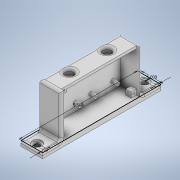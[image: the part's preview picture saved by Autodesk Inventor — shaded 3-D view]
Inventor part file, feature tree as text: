
AUTODESK INVENTOR PART (.ipt)
format: ipt  version: 2020 (Build 240168000, 168)  size: 391,680 bytes
history: native  units: in
note: dims shown in document units (in); Inventor stores cm internally (conversion verified against a paired STEP export)
features: sketch x11, extrude x7, hole x5, fillet x2, projected_geometry x2
ambient origin geometry x8: Origin, YZ Plane, XZ Plane, XY Plane, X Axis, Y Axis, Z Axis, Center Point
bodies: Solid1 (feature_tree)
feature tree (27):
  sketch  "Sketch1"  dims[d0=1.0in d1=5.5in]
  extrude  "Extrusion1"  Depth=5.5in
  hole  "Hole1"  [1 undecoded]
  extrude  "Extrusion2"  Depth=1.0in
  extrude  "Extrusion3"  Depth=0.125in
  extrude  "Extrusion4"  Depth=0.125in
  hole  "Hole2"  [1 undecoded]
  hole  "Hole3"  [1 undecoded]
  extrude  "Extrusion6"  Depth=0.125in TaperAngle=0.0deg
  extrude  "Extrusion7"  Depth=0.875in
  extrude  "Extrusion8"  Depth=0.125in
  hole  "Hole4"  [1 undecoded]
  hole  "Hole5"  [1 undecoded]
  fillet  "Fillet1"  Radius=1.125in
  fillet  "Fillet2"  Radius=0.175in
  sketch  "Sketch2"  dims[d2=0.25in d3=0.25in]
  sketch  "Sketch3"  dims[d4=0.25in d5=0.0in]
  sketch  "Sketch4"  dims[d6=0.281in d7=0.75in d8=0.438in d9=0.0625in d10=0.5635in d11=0.25in d12=0.0in d13=1.0in]
  sketch  "Sketch5"  dims[d14=0.125in d15=3.5in]
  projected_geometry  "Projected Loop1"
  sketch  "Sketch6"  dims[d16=1.0in d17=0.125in]
  projected_geometry  "Projected Loop2"
  sketch  "Sketch8"  dims[d18=1.0in d19=0.125in]
  sketch  "Sketch9"  dims[d20=2.0in d21=0.0in d22=3.5in]
  sketch  "Sketch10"  dims[d23=0.125in d24=0.75in d25=0.0in]
  sketch  "Sketch11"  dims[d26=0.9375in d27=0.875in]
  sketch  "Sketch12"  dims[d28=1.75in d29=1.025in d30=1.125in d31=1.025in d32=1.125in d33=0.175in d34=0.175in d35=0.175in d36=0.175in d37=0.175in d38=0.175in d39=0.175in d40=0.25in d41=0.0in d42=0.07in d43=0.75in d44=0.438in d45=0.25in d46=0.5635in d47=0.375in d48=0.0in d49=1.225in d50=1.325in d51=1.225in d52=1.325in d53=0.425in d54=0.425in d55=0.4in d56=0.75in d57=0.438in d58=0.25in d59=0.5635in d60=0.375in d61=0.0in d66=0.125in d67=0.125in d68=0.125in d69=0.125in d70=0.325in d71=0.25in d72=0.0in d73=0.25in d74=0.25in d75=0.25in d76=0.25in d77=0.25in d78=0.25in d79=0.0in d80=0.25in d81=0.125in d82=0.25in d83=0.25in d84=0.25in d85=0.0in d86=0.125in d87=0.125in d88=0.125in d89=0.089in d90=0.75in d91=0.438in d92=0.25in d93=0.5635in d94=0.375in d95=0.0in d96=0.125in d97=0.125in d98=0.125in d99=0.125in d100=0.125in d101=0.125in d102=0.125in d103=0.089in d104=0.75in d105=0.438in d106=0.25in d107=0.5635in d108=0.25in d109=0.0in d110=0.125in d111=0.125in d62=0.5in d63=0.0344in d64=0.5in d65=0.0344in]
note: 5 required parameter values undecoded (feature->parameter linkage not recoverable at this tier; creation-order binding heuristic only, values carry confidence <= 0.55)
